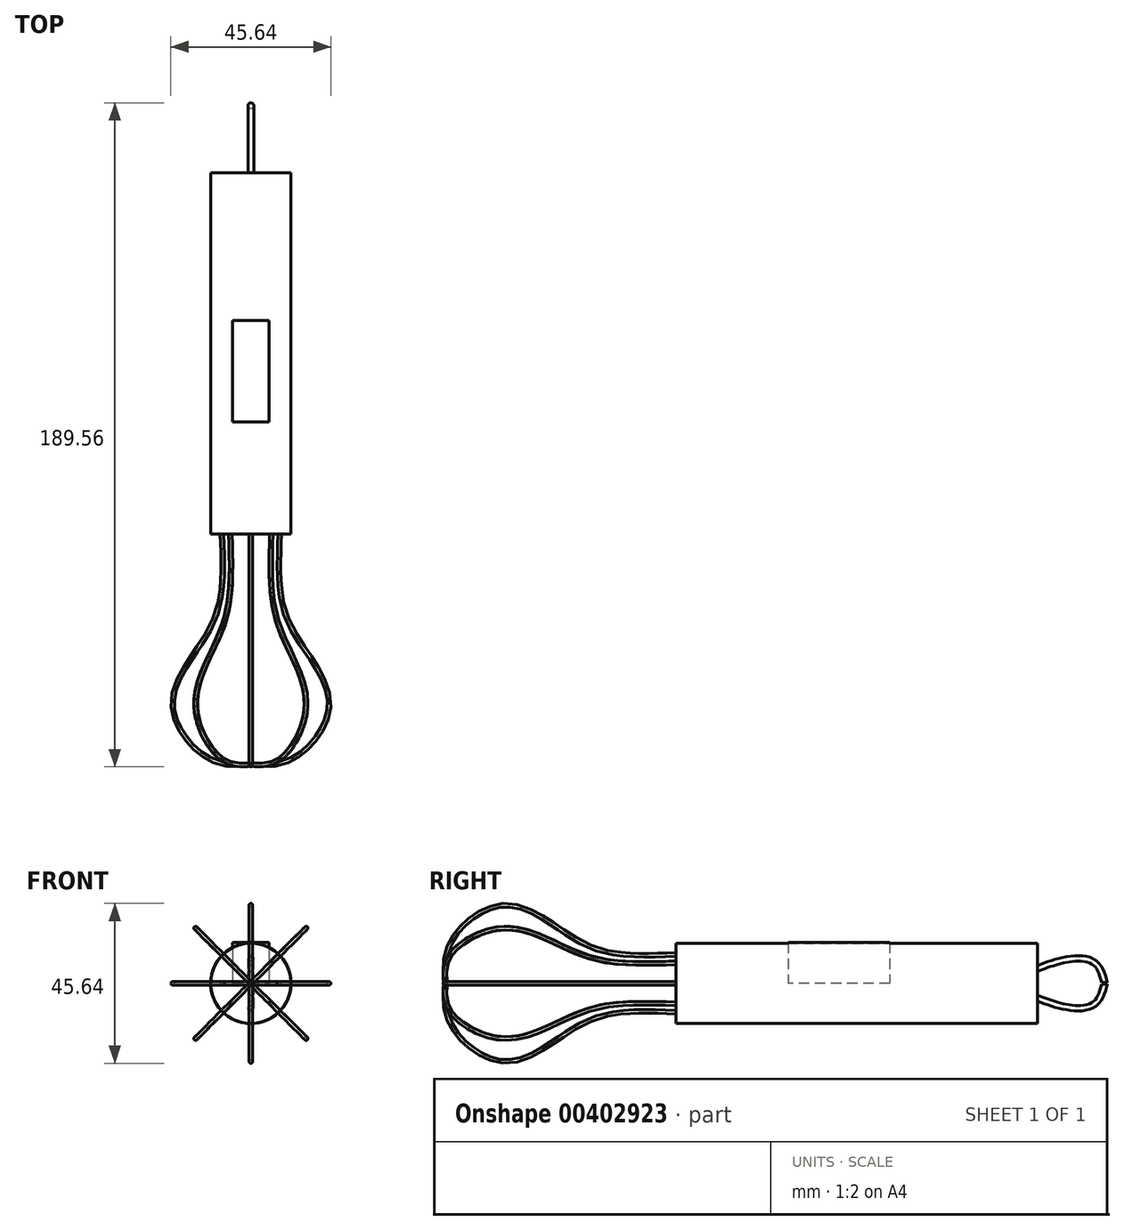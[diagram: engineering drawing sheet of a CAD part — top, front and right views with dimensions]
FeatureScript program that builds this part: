
annotation { "Feature Type Name" : "Feature", "Feature Type Description" : "" }
export const myFeature = defineFeature(function(context is Context, id is Id, definition is map)
    precondition{}
    {
        {
            var Q0;
            Q0=qCreatedBy(makeId("Front.planeOp"),FACE);
            var sketch = newSketch(context, id + "F0", { "sketchPlane" : qUnion([Q0])});
            skCircle(sketch, "E0", {"center": v(0, 0) * mm, "radius": 11.45 * mm});
            skSolve(sketch);
        }
        {
            var Q0;
            Q0 = qSketchRegion(id + "F0", true);
            extrude(context, id + "F1", {"entities" : qUnion([Q0]), "endBound" : BoundingType.SYMMETRIC, "depth" : 103.12 * mm});
        }
        {
            var Q0;
            Q0=qCreatedBy(makeId("Top.planeOp"),FACE);
            var sketch = newSketch(context, id + "F2", { "sketchPlane" : qUnion([Q0])});
            skFitSpline(sketch, "E1", {"points": [v(-8.2, -51.28) * mm, v(-9.44, -73.42) * mm, v(-17.23, -87.36) * mm, v(-22.15, -101.7) * mm, v(-11.9, -115.64) * mm, v(0, -117.28) * mm], "startDerivative": vector(4.22, -102.28) * mm, "endDerivative": vector(69.53, 4.1) * mm});
            skSolve(sketch);
        }
        {
            var Q0;
            Q0=qCreatedBy(makeId("Top.planeOp"),FACE);
            var sketch = newSketch(context, id + "F3", { "sketchPlane" : qUnion([Q0])});
            skLineSegment(sketch, "E2", {"start": v(0, 52.02) * mm, "end": v(0, -118.1) * mm});
            skSolve(sketch);
        }
        {
            var Q0;
            Q0=makeQuery(id+"F1.opExtrude","CAP_FACE",FACE,{"disambiguationData":[OSD([sQuery(id+"F0.wireOp",EDGE,"E0")])],"isStart":false});
            var sketch = newSketch(context, id + "F4", { "sketchPlane" : qUnion([Q0])});
            skCircle(sketch, "E3", {"center": v(-8.25, 0) * mm, "radius": 0.5 * mm});
            skSolve(sketch);
        }
        {
            var Q0;
            Q0=makeQuery(id+"F4.imprint","IMPRINT",FACE,{"disambiguationData":[TD([[makeQuery(id+"F4.imprint","IMPRINT",EDGE,{"derivedFrom":sQuery(id+"F4.wireOp",EDGE,"E3")}),1.0]])]});
            var Q1;
            Q1=sQuery(id+"F2.wireOp",EDGE,"E1");
            sweep(context, id + "F5", {"operationType" : NewBodyOperationType.ADD, "profiles" : qUnion([Q0]), "path" : qUnion([Q1])});
        }
        {
            var Q0;
            Q0=makeQuery(id+"F1.opExtrude","SWEPT_BODY",BODY,{"disambiguationData":[OSD([sQuery(id+"F0.wireOp",EDGE,"E0")])]});
            var Q1;
            Q1=sQuery(id+"F3.wireOp",EDGE,"E2");
            circularPattern(context, id + "F6", {"entities" : qUnion([Q0]), "axis" : qUnion([Q1]), "angle" : 360 * degree, "instanceCount" : 8, "equalSpace" : true});
        }
        {
            var Q0;
            Q0=qCreatedBy(makeId("Top.planeOp"),FACE);
            var sketch = newSketch(context, id + "F7", { "sketchPlane" : qUnion([Q0])});
            skLineSegment(sketch, "E4.bottom", {"start": v(-5.2, 9.46) * mm, "end": v(5.2, 9.46) * mm});
            skLineSegment(sketch, "E4.top", {"start": v(-5.2, -19.6) * mm, "end": v(5.2, -19.6) * mm});
            skLineSegment(sketch, "E4.left", {"start": v(-5.2, 9.46) * mm, "end": v(-5.2, -19.6) * mm});
            skLineSegment(sketch, "E4.right", {"start": v(5.2, 9.46) * mm, "end": v(5.2, -19.6) * mm});
            skPoint(sketch, "E4.middle", {"position": v(0, -5.07) * mm});
            skSolve(sketch);
        }
        {
            var Q0;
            Q0 = qSketchRegion(id + "F7", true);
            extrude(context, id + "F8", {"entities" : qUnion([Q0]), "depth" : 11.68 * mm});
        }
        {
            var Q0;
            Q0=qCreatedBy(makeId("Right.planeOp"),FACE);
            var sketch = newSketch(context, id + "F9", { "sketchPlane" : qUnion([Q0])});
            skFitSpline(sketch, "E5", {"points": [v(51.8, 4.25) * mm, v(60.02, 6.71) * mm, v(67.7, 5.9) * mm, v(70.7, 0) * mm], "startDerivative": vector(22.4, 8.38) * mm, "endDerivative": vector(6.35, -22.61) * mm});
            skSolve(sketch);
        }
        {
            var Q0;
            Q0=makeQuery(id+"F1.opExtrude","CAP_FACE",FACE,{"disambiguationData":[OSD([sQuery(id+"F0.wireOp",EDGE,"E0")])],"isStart":true});
            var sketch = newSketch(context, id + "F10", { "sketchPlane" : qUnion([Q0])});
            skCircle(sketch, "E6", {"center": v(0, 4.26) * mm, "radius": 0.83 * mm});
            skSolve(sketch);
        }
        {
            var Q0;
            Q0=qCreatedBy(makeId("Right.planeOp"),FACE);
            var sketch = newSketch(context, id + "F11", { "sketchPlane" : qUnion([Q0])});
            skLineSegment(sketch, "E7", {"start": v(70.65, 0) * mm, "end": v(-117.85, 0) * mm});
            skSolve(sketch);
        }
        {
            var Q0;
            Q0=makeQuery(id+"F10.imprint","IMPRINT",FACE,{"disambiguationData":[TD([[makeQuery(id+"F10.imprint","IMPRINT",EDGE,{"derivedFrom":sQuery(id+"F10.wireOp",EDGE,"E6")}),1.0]])]});
            var Q1;
            Q1=sQuery(id+"F9.wireOp",EDGE,"E5");
            sweep(context, id + "F12", {"profiles" : qUnion([Q0]), "path" : qUnion([Q1])});
        }
        {
            var Q0;
            Q0=makeQuery(id+"F12.opSweep","SWEPT_BODY",BODY,{"disambiguationData":[OSD([sQuery(id+"F9.wireOp",EDGE,"E5"),sQuery(id+"F10.wireOp",EDGE,"E6")])]});
            var Q1;
            Q1=sQuery(id+"F11.wireOp",EDGE,"E7");
            circularPattern(context, id + "F13", {"entities" : qUnion([Q0]), "axis" : qUnion([Q1]), "angle" : 360 * degree, "instanceCount" : 2, "equalSpace" : true});
        }
    });
